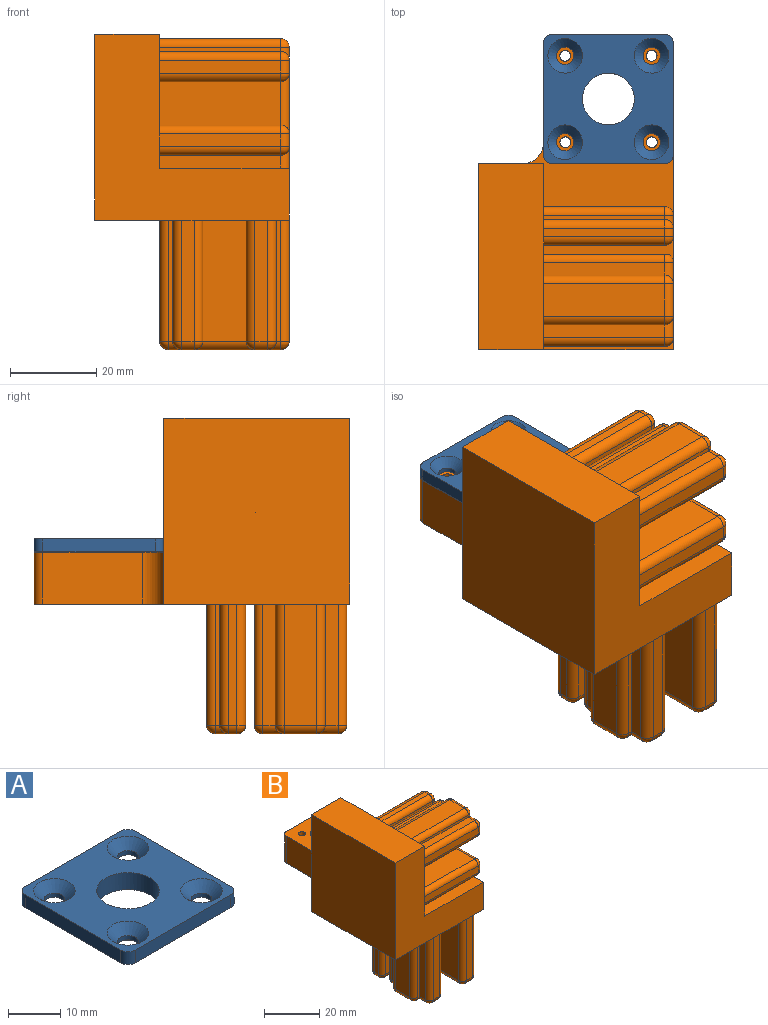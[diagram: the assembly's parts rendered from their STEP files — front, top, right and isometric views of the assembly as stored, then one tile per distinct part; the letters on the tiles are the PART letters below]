
ASSEMBLY  parts=2 mates=1
PART A: 21 faces, bbox 30x30x4 mm
  f0: plane 26x3mm, normal (0,1,0), area 78mm2, adj f4,f5,f17,f20
  f1: plane 26x3mm, normal (-1,0,0), area 78mm2, adj f4,f5,f17,f18
  f2: plane 26x3mm, normal (0,-1,0), area 78mm2, adj f4,f5,f18,f19
  f3: plane 26x3mm, normal (1,0,0), area 78mm2, adj f4,f5,f19,f20
  f4: plane 30x30mm, normal (0,0,1), area 582.4mm2, adj f0,f1,f2,f3,f10,f11,f12,f13
  f5: plane 30x30mm, normal (0,0,-1), area 469.6mm2, adj f0,f1,f2,f3,f6,f7,f8,f9
  f6: cylinder r=2mm len=4mm, axis (0,0,1), area 12.6mm2, adj f5,f13
  f7: cylinder r=2mm len=4mm, axis (0,0,1), area 12.6mm2, adj f5,f10
  f8: cylinder r=2mm len=4mm, axis (0,0,1), area 12.6mm2, adj f5,f11
  f9: cylinder r=2mm len=4mm, axis (0,0,1), area 12.6mm2, adj f5,f12
  f10: cone r=2mm half-angle=45deg, axis (0,0,1), area 53.3mm2, adj f4,f7
  f11: cone r=2mm half-angle=45deg, axis (0,0,1), area 53.3mm2, adj f4,f8
  f12: cone r=2mm half-angle=45deg, axis (0,0,1), area 53.3mm2, adj f4,f9
  f13: cone r=2mm half-angle=45deg, axis (0,0,1), area 53.3mm2, adj f4,f6
  f14: cylinder r=10.95mm len=21.9mm, axis (0,0,1), area 68.8mm2, adj f5,f15
  f15: plane 21.9x21.9mm, normal (0,0,-1), area 263.6mm2, adj f14,f16
  f16: cylinder r=6mm len=12mm, axis (0,0,1), area 150.8mm2, adj f4,f15
  f17: cylinder r=2mm len=3mm, axis (0,0,1), area 9.4mm2, adj f0,f1,f4,f5
  f18: cylinder r=2mm len=3mm, axis (0,0,-1), area 9.4mm2, adj f1,f2,f4,f5
  f19: cylinder r=2mm len=3mm, axis (0,0,1), area 9.4mm2, adj f2,f3,f4,f5
  f20: cylinder r=2mm len=3mm, axis (0,0,-1), area 9.4mm2, adj f0,f3,f4,f5
PART B: 187 faces, bbox 45x73x73 mm
  f0: cylinder r=2mm len=28mm, axis (0,0,1), area 62.7mm2, adj f1,f13,f53,f184
  f1: sphere r=2mm, area 5.7mm2, adj f0,f2,f70,f184
  f2: cylinder r=2mm len=3mm, axis (-1,0,0), area 6.7mm2, adj f1,f3,f57,f184
  f3: sphere r=2mm, area 5.7mm2, adj f2,f4,f72,f184
  f4: cylinder r=2mm len=28mm, axis (0,0,1), area 62.7mm2, adj f3,f13,f52,f184
  f5: cylinder r=2mm len=28mm, axis (0,0,1), area 62.7mm2, adj f6,f13,f77,f183
  f6: sphere r=2mm, area 5.7mm2, adj f5,f7,f80,f183
  f7: cylinder r=2mm len=3mm, axis (-1,0,0), area 6.7mm2, adj f6,f9,f79,f183
  f8: cylinder r=2mm len=28mm, axis (0,0,1), area 62.7mm2, adj f9,f13,f76,f183
  f9: sphere r=2mm, area 5.7mm2, adj f7,f8,f87,f183
  f10: plane 43x31mm, normal (1,0,0), area 799.6mm2, adj f11,f16,f18,f95,f96,f99,f100,f101
  f11: plane 30x7.7mm, normal (0,0,1), area 171.9mm2, adj f10,f16,f17,f104,f105
  f12: plane 23x12mm, normal (-1,0,0), area 276mm2, adj f13,f18,f98,f120
  f13: plane 73x45mm, normal (0,0,-1), area 2174.2mm2, adj f0,f4,f5,f8,f12,f14,f15,f16
  f14: plane 26x12mm, normal (0,1,0), area 312mm2, adj f13,f18,f120,f121
  f15: plane 28x7.5mm, normal (-1,0,0), area 210mm2, adj f13,f60,f66,f67
  f16: plane 45x43mm, normal (0,-1,0), area 1005mm2, adj f10,f11,f13,f17,f96,f97
  f17: plane 71x48mm, normal (1,0,0), area 1152mm2, adj f11,f13,f16,f18,f81,f84,f85,f105
  f18: plane 57.8x35mm, normal (0,0,1), area 1282.2mm2, adj f10,f12,f14,f17,f19,f95,f98,f99
  f19: cylinder r=10.95mm len=21.9mm, axis (0,0,1), area 550.4mm2, adj f18,f20
  f20: plane 21.9x21.9mm, normal (0,0,1), area 263.6mm2, adj f19,f21
  f21: cylinder r=6mm len=12mm, axis (0,0,1), area 150.8mm2, adj f13,f20
  f22: plane 28x2mm, normal (1,0,0), area 56mm2, adj f13,f35,f39,f41
  f23: plane 28x20mm, normal (0,-1,0), area 560mm2, adj f13,f33,f41,f43
  f24: plane 28x2mm, normal (-1,0,0), area 56mm2, adj f13,f31,f43,f45
  f25: plane 28x4.2mm, normal (0,1,0), area 117.6mm2, adj f13,f26,f32,f45
  f26: plane 28x1mm, normal (-1,0,0), area 28mm2, adj f13,f25,f34,f47
  f27: plane 28x7.6mm, normal (0,1,0), area 212.8mm2, adj f13,f36,f47,f49
  f28: plane 28x1mm, normal (1,0,0), area 28mm2, adj f13,f29,f38,f49
  f29: plane 28x4.2mm, normal (0,1,0), area 117.6mm2, adj f13,f28,f37,f39
  f30: plane 20x5mm, normal (0,0,-1), area 62.8mm2, adj f31,f32,f33,f34,f35,f36,f37,f38
  f31: cylinder r=2mm len=2mm, axis (0,-1,0), area 6.3mm2, adj f24,f30,f44,f46
  f32: cylinder r=2mm len=6.2mm, axis (-1,0,0), area 15.5mm2, adj f25,f30,f34,f46
  f33: cylinder r=2mm len=20mm, axis (1,0,0), area 62.8mm2, adj f23,f30,f42,f44
  f34: cylinder r=2mm len=3mm, axis (0,-1,0), area 5.4mm2, adj f26,f30,f32,f48
  f35: cylinder r=2mm len=2mm, axis (0,1,0), area 6.3mm2, adj f22,f30,f40,f42
  f36: cylinder r=2mm len=7.6mm, axis (-1,0,0), area 23.9mm2, adj f27,f30,f48,f50
  f37: cylinder r=2mm len=6.2mm, axis (-1,0,0), area 15.5mm2, adj f29,f30,f38,f40
  f38: cylinder r=2mm len=3mm, axis (0,1,0), area 5.4mm2, adj f28,f30,f37,f50
  f39: cylinder r=2mm len=28mm, axis (0,0,1), area 88mm2, adj f13,f22,f29,f40
  f40: sphere r=2mm, area 6.3mm2, adj f35,f37,f39
  f41: cylinder r=2mm len=28mm, axis (0,0,1), area 88mm2, adj f13,f22,f23,f42
  f42: sphere r=2mm, area 6.3mm2, adj f33,f35,f41
  f43: cylinder r=2mm len=28mm, axis (0,0,1), area 88mm2, adj f13,f23,f24,f44
  f44: sphere r=2mm, area 6.3mm2, adj f31,f33,f43
  f45: cylinder r=2mm len=28mm, axis (0,0,1), area 88mm2, adj f13,f24,f25,f46
  f46: sphere r=2mm, area 6.3mm2, adj f31,f32,f45
  f47: cylinder r=2mm len=28mm, axis (0,0,1), area 88mm2, adj f13,f26,f27,f48
  f48: sphere r=2mm, area 6.3mm2, adj f34,f36,f47
  f49: cylinder r=2mm len=28mm, axis (0,0,1), area 88mm2, adj f13,f27,f28,f50
  f50: sphere r=2mm, area 6.3mm2, adj f36,f38,f49
  f51: plane 28x1mm, normal (0,1,0), area 28mm2, adj f13,f52,f66,f71
  f52: plane 28x3mm, normal (-1,0,0), area 84mm2, adj f4,f13,f51,f72
  f53: plane 28x17.5mm, normal (1,0,0), area 490mm2, adj f0,f13,f65,f70
  f54: plane 28x3mm, normal (0,-1,0), area 84mm2, adj f13,f59,f64,f65
  f55: plane 28x3mm, normal (-1,0,0), area 84mm2, adj f13,f56,f58,f59
  f56: plane 28x1mm, normal (0,-1,0), area 28mm2, adj f13,f55,f60,f61
  f57: plane 17.5x6mm, normal (0,0,-1), area 75mm2, adj f2,f58,f61,f64,f67,f70,f71,f72
  f58: cylinder r=2mm len=5mm, axis (0,-1,0), area 11.7mm2, adj f55,f57,f61,f62
  f59: cylinder r=2mm len=28mm, axis (0,0,1), area 88mm2, adj f13,f54,f55,f62
  f60: cylinder r=2mm len=28mm, axis (0,0,-1), area 88mm2, adj f13,f15,f56,f63
  f61: cylinder r=2mm len=3mm, axis (1,0,0), area 5.4mm2, adj f56,f57,f58,f63
  f62: sphere r=2mm, area 6.3mm2, adj f58,f59,f64
  f63: sphere r=2mm, area 6.3mm2, adj f60,f61,f67
  f64: cylinder r=2mm len=3mm, axis (1,0,0), area 9.4mm2, adj f54,f57,f62,f68
  f65: cylinder r=2mm len=28mm, axis (0,0,1), area 88mm2, adj f13,f53,f54,f68
  f66: cylinder r=2mm len=28mm, axis (0,0,-1), area 88mm2, adj f13,f15,f51,f69
  f67: cylinder r=2mm len=7.5mm, axis (0,1,0), area 23.6mm2, adj f15,f57,f63,f69
  f68: sphere r=2mm, area 6.3mm2, adj f64,f65,f70
  f69: sphere r=2mm, area 6.3mm2, adj f66,f67,f71
  f70: cylinder r=2mm len=17.5mm, axis (0,1,0), area 55mm2, adj f1,f53,f57,f68
  f71: cylinder r=2mm len=3mm, axis (-1,0,0), area 5.4mm2, adj f51,f57,f69,f72
  f72: cylinder r=2mm len=5mm, axis (0,-1,0), area 11.7mm2, adj f3,f52,f57,f71
  f73: plane 28x1mm, normal (0,-1,0), area 28mm2, adj f13,f74,f84,f89
  f74: plane 28x3mm, normal (1,0,0), area 84mm2, adj f13,f73,f91,f94
  f75: plane 28x3mm, normal (0,-1,0), area 84mm2, adj f13,f88,f92,f94
  f76: plane 28x17.5mm, normal (-1,0,0), area 490mm2, adj f8,f13,f87,f88
  f77: plane 28x3mm, normal (1,0,0), area 84mm2, adj f5,f13,f78,f80
  f78: plane 28x1mm, normal (0,1,0), area 28mm2, adj f13,f77,f81,f82
  f79: plane 17.5x6mm, normal (0,0,-1), area 75mm2, adj f7,f80,f82,f85,f87,f89,f91,f92
  f80: cylinder r=2mm len=5mm, axis (0,1,0), area 11.7mm2, adj f6,f77,f79,f82
  f81: cylinder r=2mm len=28mm, axis (0,0,1), area 88mm2, adj f13,f17,f78,f83
  f82: cylinder r=2mm len=3mm, axis (-1,0,0), area 5.4mm2, adj f78,f79,f80,f83
  f83: sphere r=2mm, area 6.3mm2, adj f81,f82,f85
  f84: cylinder r=2mm len=28mm, axis (0,0,1), area 88mm2, adj f13,f17,f73,f86
  f85: cylinder r=2mm len=7.5mm, axis (0,-1,0), area 23.6mm2, adj f17,f79,f83,f86
  f86: sphere r=2mm, area 6.3mm2, adj f84,f85,f89
  f87: cylinder r=2mm len=17.5mm, axis (0,-1,0), area 55mm2, adj f9,f76,f79,f90
  f88: cylinder r=2mm len=28mm, axis (0,0,1), area 88mm2, adj f13,f75,f76,f90
  f89: cylinder r=2mm len=3mm, axis (1,0,0), area 5.4mm2, adj f73,f79,f86,f91
  f90: sphere r=2mm, area 6.3mm2, adj f87,f88,f92
  f91: cylinder r=2mm len=5mm, axis (0,1,0), area 11.7mm2, adj f74,f79,f89,f93
  f92: cylinder r=2mm len=3mm, axis (1,0,0), area 9.4mm2, adj f75,f79,f90,f93
  f93: sphere r=2mm, area 6.3mm2, adj f91,f92,f94
  f94: cylinder r=2mm len=28mm, axis (0,0,1), area 88mm2, adj f13,f74,f75,f93
  f95: plane 43x15mm, normal (0,1,0), area 585mm2, adj f10,f13,f18,f96,f97,f98
  f96: plane 43x15mm, normal (0,0,1), area 645mm2, adj f10,f16,f95,f97
  f97: plane 43x43mm, normal (-1,0,0), area 1849mm2, adj f13,f16,f95,f96
  f98: cylinder r=5mm len=12mm, axis (0,0,1), area 94.2mm2, adj f12,f13,f18,f95
  f99: plane 28x3mm, normal (0,1,0), area 84mm2, adj f10,f18,f100,f114
  f100: plane 28x3mm, normal (0,0,-1), area 84mm2, adj f10,f99,f116,f119
  f101: plane 28x17.5mm, normal (0,0,1), area 490mm2, adj f10,f110,f112,f113
  f102: plane 28x3mm, normal (0,-1,0), area 84mm2, adj f10,f107,f109,f110
  f103: plane 28x3mm, normal (0,0,-1), area 84mm2, adj f10,f104,f106,f107
  f104: plane 28x3mm, normal (0,-1,0), area 84mm2, adj f10,f11,f103,f105
  f105: cylinder r=2mm len=5mm, axis (0,0,1), area 11.7mm2, adj f11,f17,f104,f106
  f106: cylinder r=2mm len=5mm, axis (0,-1,0), area 11.7mm2, adj f17,f103,f105,f108
  f107: cylinder r=2mm len=28mm, axis (-1,0,0), area 88mm2, adj f10,f102,f103,f108
  f108: sphere r=2mm, area 6.3mm2, adj f106,f107,f109
  f109: cylinder r=2mm len=3mm, axis (0,0,1), area 9.4mm2, adj f17,f102,f108,f111
  f110: cylinder r=2mm len=28mm, axis (-1,0,0), area 88mm2, adj f10,f101,f102,f111
  f111: sphere r=2mm, area 6.3mm2, adj f109,f110,f112
  f112: cylinder r=2mm len=17.5mm, axis (0,1,0), area 55mm2, adj f17,f101,f111,f115
  f113: cylinder r=2mm len=28mm, axis (-1,0,0), area 62.7mm2, adj f10,f101,f115,f186
  f114: cylinder r=2mm len=5mm, axis (0,0,-1), area 11.7mm2, adj f17,f18,f99,f116
  f115: sphere r=2mm, area 5.7mm2, adj f112,f113,f117,f186
  f116: cylinder r=2mm len=5mm, axis (0,-1,0), area 11.7mm2, adj f17,f100,f114,f118
  f117: cylinder r=2mm len=3mm, axis (0,0,-1), area 6.7mm2, adj f17,f115,f118,f186
  f118: sphere r=2mm, area 5.7mm2, adj f116,f117,f119,f186
  f119: cylinder r=2mm len=28mm, axis (-1,0,0), area 62.7mm2, adj f10,f100,f118,f186
  f120: cylinder r=2mm len=12mm, axis (0,0,1), area 37.7mm2, adj f12,f13,f14,f18
  f121: cylinder r=2mm len=12mm, axis (0,0,-1), area 37.7mm2, adj f13,f14,f17,f18
  f122: plane 28x3mm, normal (0,-1,0), area 84mm2, adj f10,f140,f146,f149
  f123: plane 28x17.5mm, normal (0,0,-1), area 490mm2, adj f10,f143,f147,f149
  f124: plane 28x3mm, normal (0,0,1), area 84mm2, adj f10,f125,f136,f137
  f125: plane 28x1mm, normal (0,1,0), area 28mm2, adj f10,f124,f130,f134
  f126: plane 28x7.5mm, normal (0,0,1), area 210mm2, adj f10,f130,f132,f133
  f127: plane 28x1mm, normal (0,-1,0), area 28mm2, adj f10,f128,f132,f138
  f128: plane 28x3mm, normal (0,0,1), area 84mm2, adj f10,f127,f140,f141
  f129: plane 17.5x6mm, normal (1,0,0), area 75mm2, adj f133,f134,f136,f138,f141,f142,f146,f147
  f130: cylinder r=2mm len=28mm, axis (-1,0,0), area 88mm2, adj f10,f125,f126,f131
  f131: sphere r=2mm, area 6.3mm2, adj f130,f133,f134
  f132: cylinder r=2mm len=28mm, axis (-1,0,0), area 88mm2, adj f10,f126,f127,f135
  f133: cylinder r=2mm len=7.5mm, axis (0,1,0), area 23.6mm2, adj f126,f129,f131,f135
  f134: cylinder r=2mm len=3mm, axis (0,0,-1), area 5.4mm2, adj f125,f129,f131,f136
  f135: sphere r=2mm, area 6.3mm2, adj f132,f133,f138
  f136: cylinder r=2mm len=5mm, axis (0,1,0), area 11.7mm2, adj f124,f129,f134,f139
  f137: cylinder r=2mm len=28mm, axis (-1,0,0), area 62.7mm2, adj f10,f124,f139,f185
  f138: cylinder r=2mm len=3mm, axis (0,0,1), area 5.4mm2, adj f127,f129,f135,f141
  f139: sphere r=2mm, area 5.7mm2, adj f136,f137,f142,f185
  f140: cylinder r=2mm len=28mm, axis (-1,0,0), area 88mm2, adj f10,f122,f128,f144
  f141: cylinder r=2mm len=5mm, axis (0,1,0), area 11.7mm2, adj f128,f129,f138,f144
  f142: cylinder r=2mm len=3mm, axis (0,0,-1), area 6.7mm2, adj f129,f139,f145,f185
  f143: cylinder r=2mm len=28mm, axis (-1,0,0), area 62.7mm2, adj f10,f123,f145,f185
  f144: sphere r=2mm, area 6.3mm2, adj f140,f141,f146
  f145: sphere r=2mm, area 5.7mm2, adj f142,f143,f147,f185
  f146: cylinder r=2mm len=3mm, axis (0,0,1), area 9.4mm2, adj f122,f129,f144,f148
  f147: cylinder r=2mm len=17.5mm, axis (0,-1,0), area 55mm2, adj f123,f129,f145,f148
  f148: sphere r=2mm, area 6.3mm2, adj f146,f147,f149
  f149: cylinder r=2mm len=28mm, axis (-1,0,0), area 88mm2, adj f10,f122,f123,f148
  f150: plane 28x2mm, normal (0,0,1), area 56mm2, adj f10,f169,f175,f178
  f151: plane 28x20mm, normal (0,-1,0), area 560mm2, adj f10,f172,f176,f178
  f152: plane 28x2mm, normal (0,0,-1), area 56mm2, adj f10,f166,f171,f172
  f153: plane 28x4.2mm, normal (0,1,0), area 117.6mm2, adj f10,f154,f165,f166
  f154: plane 28x1mm, normal (0,0,-1), area 28mm2, adj f10,f153,f159,f163
  f155: plane 28x7.6mm, normal (0,1,0), area 212.8mm2, adj f10,f159,f161,f162
  f156: plane 28x1mm, normal (0,0,1), area 28mm2, adj f10,f157,f161,f167
  f157: plane 28x4.2mm, normal (0,1,0), area 117.6mm2, adj f10,f156,f169,f170
  f158: plane 20x5mm, normal (1,0,0), area 62.8mm2, adj f162,f163,f165,f167,f170,f171,f175,f176
  f159: cylinder r=2mm len=28mm, axis (-1,0,0), area 88mm2, adj f10,f154,f155,f160
  f160: sphere r=2mm, area 6.3mm2, adj f159,f162,f163
  f161: cylinder r=2mm len=28mm, axis (-1,0,0), area 88mm2, adj f10,f155,f156,f164
  f162: cylinder r=2mm len=7.6mm, axis (0,0,-1), area 23.9mm2, adj f155,f158,f160,f164
  f163: cylinder r=2mm len=3mm, axis (0,-1,0), area 5.4mm2, adj f154,f158,f160,f165
  f164: sphere r=2mm, area 6.3mm2, adj f161,f162,f167
  f165: cylinder r=2mm len=6.2mm, axis (0,0,-1), area 15.5mm2, adj f153,f158,f163,f168
  f166: cylinder r=2mm len=28mm, axis (-1,0,0), area 88mm2, adj f10,f152,f153,f168
  f167: cylinder r=2mm len=3mm, axis (0,1,0), area 5.4mm2, adj f156,f158,f164,f170
  f168: sphere r=2mm, area 6.3mm2, adj f165,f166,f171
  f169: cylinder r=2mm len=28mm, axis (-1,0,0), area 88mm2, adj f10,f150,f157,f173
  f170: cylinder r=2mm len=6.2mm, axis (0,0,-1), area 15.5mm2, adj f157,f158,f167,f173
  f171: cylinder r=2mm len=2mm, axis (0,-1,0), area 6.3mm2, adj f152,f158,f168,f174
  f172: cylinder r=2mm len=28mm, axis (-1,0,0), area 88mm2, adj f10,f151,f152,f174
  f173: sphere r=2mm, area 6.3mm2, adj f169,f170,f175
  f174: sphere r=2mm, area 6.3mm2, adj f171,f172,f176
  f175: cylinder r=2mm len=2mm, axis (0,1,0), area 6.3mm2, adj f150,f158,f173,f177
  f176: cylinder r=2mm len=20mm, axis (0,0,1), area 62.8mm2, adj f151,f158,f174,f177
  f177: sphere r=2mm, area 6.3mm2, adj f175,f176,f178
  f178: cylinder r=2mm len=28mm, axis (-1,0,0), area 88mm2, adj f10,f150,f151,f177
  f179: cylinder r=1.25mm len=12mm, axis (0,0,1), area 94.2mm2, adj f13,f18
  f180: cylinder r=1.25mm len=12mm, axis (0,0,1), area 94.2mm2, adj f13,f18
  f181: cylinder r=1.25mm len=12mm, axis (0,0,1), area 94.2mm2, adj f13,f18
  f182: cylinder r=1.25mm len=12mm, axis (0,0,1), area 94.2mm2, adj f13,f18
  f183: plane 28.87x4.74mm, normal (0,1,0), area 136.6mm2, adj f5,f6,f7,f8,f9,f13
  f184: plane 28.87x4.74mm, normal (0,1,0), area 136.6mm2, adj f0,f1,f2,f3,f4,f13
  f185: plane 28.87x4.74mm, normal (0,1,0), area 136.6mm2, adj f10,f137,f139,f142,f143,f145
  f186: plane 28.87x4.74mm, normal (0,1,0), area 136.6mm2, adj f10,f113,f115,f117,f118,f119
PLACE A t=(-28.35,3.06,8.99)mm
PLACE B t=(-28.35,-14.16,-3.11)mm
MATE fastened A.f20 <-> B.f121  axis (0,0,-1) through (-15.35,16.06,8.99)mm
